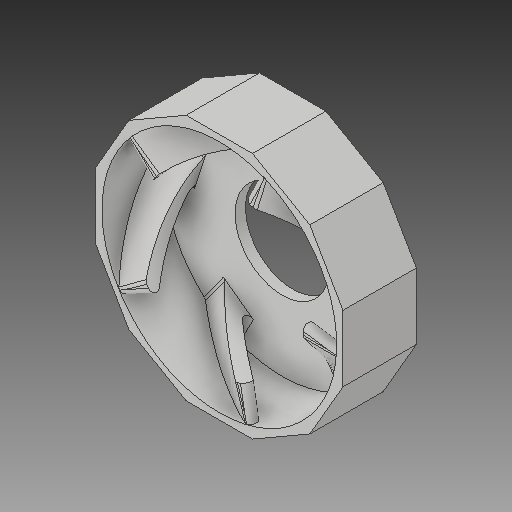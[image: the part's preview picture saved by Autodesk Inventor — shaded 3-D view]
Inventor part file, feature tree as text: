
AUTODESK INVENTOR PART (.ipt)
format: ipt  version: 2018 (Build 220112000, 112)  size: 609,280 bytes
history: native  units: in
note: dims shown in document units (in); Inventor stores cm internally (conversion verified against a paired STEP export)
features: sketch x3, extrude x2, fillet x2, helix x1, pattern_circular x1, projected_geometry x1
ambient origin geometry x8: Origin, YZ Plane, XZ Plane, XY Plane, X Axis, Y Axis, Z Axis, Center Point
bodies: Solid1 (feature_tree)
feature tree (10):
  extrude  "Extrusion1"  Depth=0.75in TaperAngle=0.0deg
  extrude  "Extrusion2"  Depth=0.12in
  helix  "Coil1"  [1 undecoded]
  fillet  "Fillet1"  Radius=0.0625in
  fillet  "Fillet2"  Radius=2.95in
  pattern_circular  "Circular Pattern2"  [2 undecoded]
  sketch  "Sketch1"  dims[d0=0.125in d1=0.0in d2=0.75in d3=0.0in]
  sketch  "Sketch2"  dims[d4=0.12in d5=0.12in d6=1.0in]
  projected_geometry  "Projected Loop1"
  sketch  "Sketch3"  dims[d7=5.0in d8=0.75in d9=0.3937in d10=0.0in d11=90.0deg d12=90.0deg d13=0.0in d14=0.0in d15=0.0625in d19=2.95in d20=1.125in d21=2.8in d22=0.0625in d23=1.9685in d24=360.0deg d26=0.45in]
note: 3 required parameter values undecoded (feature->parameter linkage not recoverable at this tier; creation-order binding heuristic only, values carry confidence <= 0.55)
